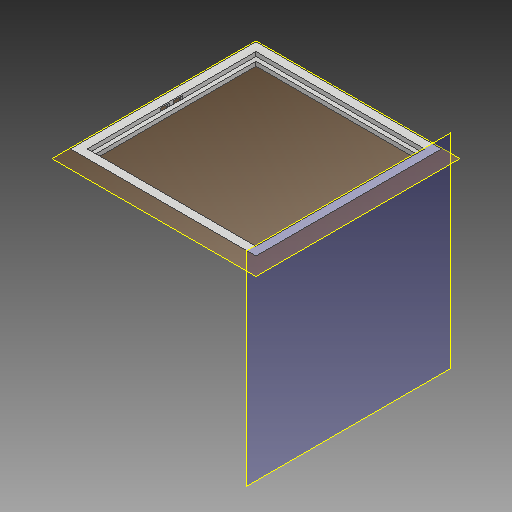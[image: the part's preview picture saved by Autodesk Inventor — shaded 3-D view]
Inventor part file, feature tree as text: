
AUTODESK INVENTOR PART (.ipt)
format: ipt  version: 2018.3 (Build 223284000, 284)  size: 169,472 bytes
history: native  units: mm
features: reference x19, other x10, extrude x4, sketch x4, plane x2, chamfer x1
ambient origin geometry x8: Origin, YZ Plane, XZ Plane, XY Plane, X Axis, Y Axis, Z Axis, Center Point
bodies: Volumenkörper1 (feature_tree)
feature tree (40):
  extrude  "Extrusion1"  Depth=20.0mm TaperAngle=45.0deg
  chamfer  "Fase1"  Distance=17.0mm
  plane  "Arbeitsebene1"
  extrude  "Extrusion2"  Depth=10.0mm
  extrude  "Extrusion3"  Depth=10.0mm
  plane  "Arbeitsebene3"
  extrude  "Extrusion4"  Depth=10.0mm TaperAngle=0.0deg
  sketch  "Skizze1"  dims[d0=20.0mm d1=0.0mm d2=20.0mm d3=2.0mm d4=45.0deg]
  reference  "Referenz1"
  reference  "Referenz2"
  reference  "Referenz3"
  reference  "Referenz4"
  reference  "Referenz5"
  sketch  "Skizze3"  dims[d5=-20.0mm d6=17.0mm d7=0.0mm]
  reference  "Referenz12"
  reference  "Referenz13"
  reference  "Referenz14"
  reference  "Referenz15"
  reference  "Referenz16"
  reference  "Referenz17"
  reference  "Referenz18"
  reference  "Referenz19"
  sketch  "Skizze5"  dims[d8=10.0mm d9=10.0mm]
  sketch  "Skizze6"  dims[d10=10.0mm d11=10.0mm d12=10.0mm d13=0.0mm d14=25.0mm d15=0.0mm]
  reference  "Referenz20"
  reference  "Referenz21"
  reference  "Referenz22"
  reference  "Referenz23"
  reference  "Referenz24"
  reference  "Referenz25"
  parser-record x1  (decoder bookkeeping rows leaked as tree rows — omitted from the tree; the rows remain in map.json)
  other  "SmartCube_Quadratisch.iam"
  other  "Wand2_MIR:1"
  other  "Wand1:1"
  other  "Wand1_MIR:1"
  other  "Wand2:1"
  other  "PV_Modul:1"
  other  "<userpath>\Documents\Dipl\Smartcube_Construction\Version_3\Baugruppe1.iam"
  other  "Baugruppe1.iam"
  other  "PV_Ramen_CPY_3_2:1"
note: 1 file-system path scrubbed to <path> (originals preserved in map.json)
